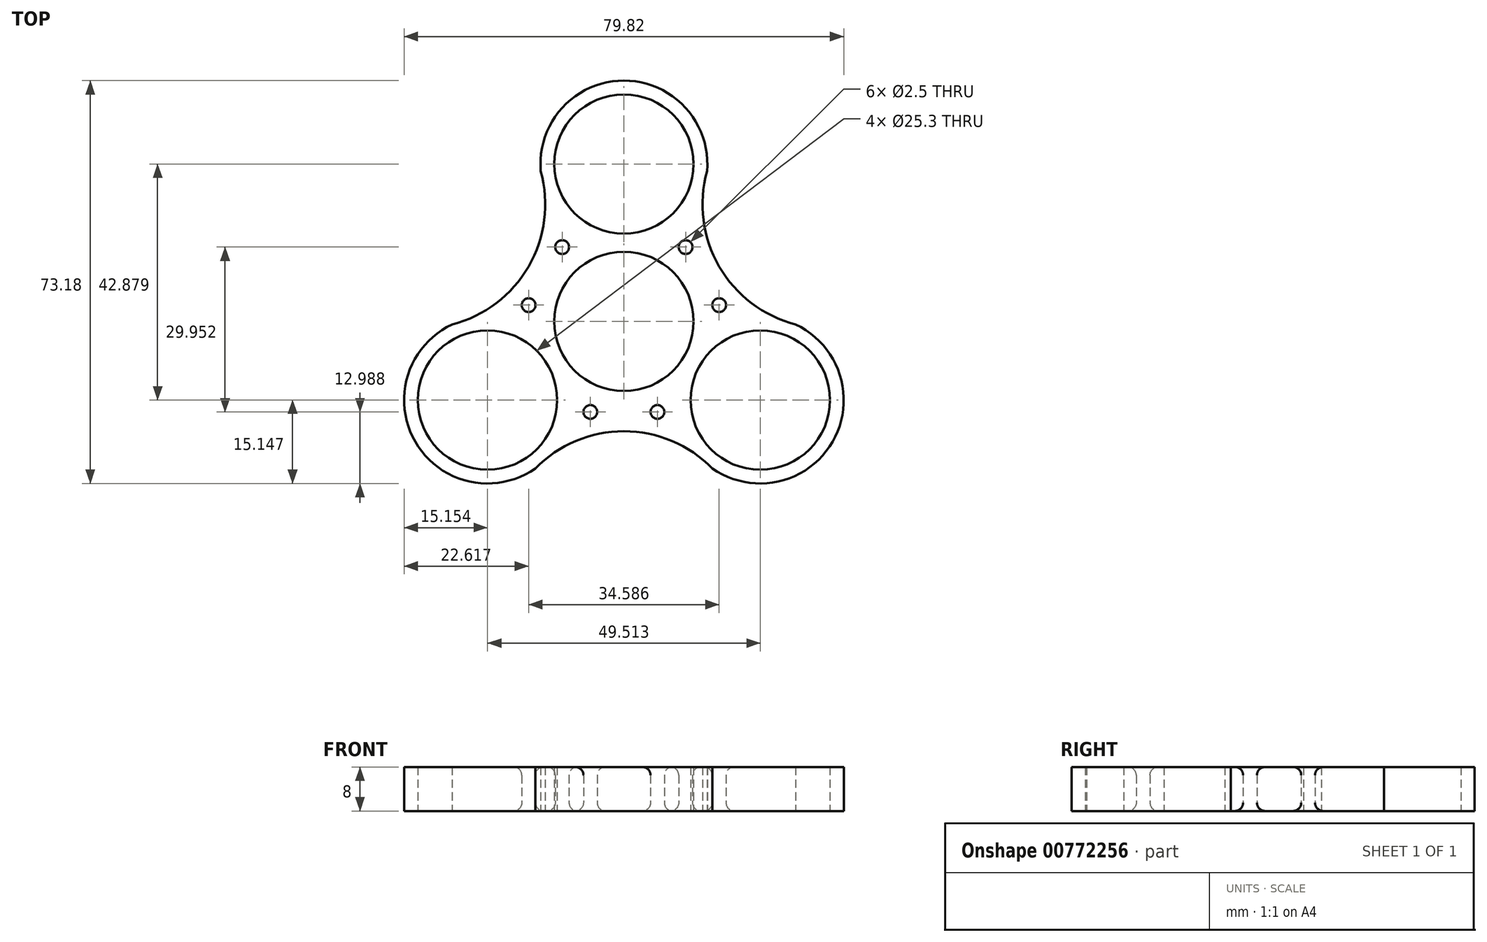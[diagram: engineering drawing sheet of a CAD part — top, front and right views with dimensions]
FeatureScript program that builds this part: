
annotation { "Feature Type Name" : "Feature", "Feature Type Description" : "" }
export const myFeature = defineFeature(function(context is Context, id is Id, definition is map)
    precondition{}
    {
        {
            var Q0;
            Q0=qCreatedBy(makeId("Top.planeOp"),FACE);
            var sketch = newSketch(context, id + "F0", { "sketchPlane" : qUnion([Q0])});
            skCircle(sketch, "E0", {"center": v(0, 0) * mm, "radius": 12.65 * mm});
            skCircle(sketch, "E1", {"center": v(0, 28.59) * mm, "radius": 12.65 * mm});
            skArc(sketch, "E2", {"start": v(14.44, 24.01) * mm, "mid": v(0, 43.74) * mm, "end": v(-14.44, 24.01) * mm});
            skPoint(sketch, "E3.start.orphan", {"position": v(-15.15, 0) * mm});
            skCircle(sketch, "E4.1.0", {"center": v(-24.76, -14.3) * mm, "radius": 12.65 * mm});
            skArc(sketch, "E4.1.1", {"start": v(-28.02, 0.5) * mm, "mid": v(-37.88, -21.87) * mm, "end": v(-13.58, -24.52) * mm});
            skCircle(sketch, "E4.2.0", {"center": v(24.76, -14.3) * mm, "radius": 12.65 * mm});
            skArc(sketch, "E4.2.1", {"start": v(13.58, -24.52) * mm, "mid": v(37.88, -21.87) * mm, "end": v(28.02, 0.5) * mm});
            skLineSegment(sketch, "E5", {"start": v(-14.89, -2.8) * mm, "end": v(-5.02, 14.3) * mm, "construction": true});
            skLineSegment(sketch, "E6", {"start": v(-9.96, 5.75) * mm, "end": v(-23.13, 13.35) * mm, "construction": true});
            skLineSegment(sketch, "E7", {"start": v(-23.13, 13.35) * mm, "end": v(-15.1, 27.27) * mm, "construction": true});
            skLineSegment(sketch, "E8", {"start": v(-23.13, 13.35) * mm, "end": v(-31.17, -0.57) * mm, "construction": true});
            skArc(sketch, "E9", {"start": v(-31.17, -0.57) * mm, "mid": v(-17.3, 9.98) * mm, "end": v(-15.1, 27.27) * mm});
            skArc(sketch, "E10.1.0", {"start": v(16.07, -26.7) * mm, "mid": v(0, -19.97) * mm, "end": v(-16.07, -26.7) * mm});
            skArc(sketch, "E10.2.0", {"start": v(15.1, 27.27) * mm, "mid": v(17.3, 9.98) * mm, "end": v(31.17, -0.57) * mm});
            skPoint(sketch, "E11.center.orphan", {"position": v(-17.3, 9.98) * mm});
            skLineSegment(sketch, "E12", {"start": v(-17.3, 9.98) * mm, "end": v(-17.3, -4.08) * mm, "construction": true});
            skCircle(sketch, "E13", {"center": v(-17.3, 2.95) * mm, "radius": 1.25 * mm});
            skCircle(sketch, "E14.1.0", {"center": v(6.09, -16.45) * mm, "radius": 1.25 * mm});
            skCircle(sketch, "E14.2.0", {"center": v(11.2, 13.5) * mm, "radius": 1.25 * mm});
            skLineSegment(sketch, "E15", {"start": v(-17.3, 2.95) * mm, "end": v(23.66, 2.95) * mm, "construction": true});
            skArc(sketch, "E16", {"start": v(17.3, 8.66) * mm, "mid": v(17.65, 8.71) * mm, "end": v(17.99, 8.86) * mm});
            skLineSegment(sketch, "E17", {"start": v(17.3, 9.98) * mm, "end": v(17.3, 2.95) * mm, "construction": true});
            skCircle(sketch, "E18", {"center": v(17.3, 2.95) * mm, "radius": 1.25 * mm});
            skCircle(sketch, "E19.1.0", {"center": v(-11.2, 13.5) * mm, "radius": 1.25 * mm});
            skCircle(sketch, "E19.2.0", {"center": v(-6.09, -16.45) * mm, "radius": 1.25 * mm});
            skSolve(sketch);
        }
        {
            var Q0;
            Q0=makeQuery(id+"F0.imprint","IMPRINT",FACE,{"disambiguationData":[TD([[makeQuery(id+"F0.imprint","IMPRINT",EDGE,{"derivedFrom":sQuery(id+"F0.wireOp",EDGE,"E0")}),-1.0]])]});
            extrude(context, id + "F1", {"entities" : qUnion([Q0]), "depth" : 8 * mm, "offsetDistance" : 25 * mm});
        }
        {
            var Q0;
            Q0=makeQuery(id+"F1.opExtrude","CAP_EDGE",EDGE,{"disambiguationData":[OSD([sQuery(id+"F0.wireOp",EDGE,"E19.1.0")])],"isStart":true});
            var Q1;
            Q1=makeQuery(id+"F1.opExtrude","CAP_EDGE",EDGE,{"disambiguationData":[OSD([sQuery(id+"F0.wireOp",EDGE,"E19.1.0")])],"isStart":false});
            var Q2;
            Q2=makeQuery(id+"F1.opExtrude","CAP_EDGE",EDGE,{"disambiguationData":[OSD([sQuery(id+"F0.wireOp",EDGE,"E13")])],"isStart":false});
            var Q3;
            Q3=makeQuery(id+"F1.opExtrude","CAP_EDGE",EDGE,{"disambiguationData":[OSD([sQuery(id+"F0.wireOp",EDGE,"E19.2.0")])],"isStart":false});
            var Q4;
            Q4=makeQuery(id+"F1.opExtrude","CAP_EDGE",EDGE,{"disambiguationData":[OSD([sQuery(id+"F0.wireOp",EDGE,"E14.1.0")])],"isStart":false});
            var Q5;
            Q5=makeQuery(id+"F1.opExtrude","CAP_EDGE",EDGE,{"disambiguationData":[OSD([sQuery(id+"F0.wireOp",EDGE,"E18")])],"isStart":false});
            var Q6;
            Q6=makeQuery(id+"F1.opExtrude","CAP_EDGE",EDGE,{"disambiguationData":[OSD([sQuery(id+"F0.wireOp",EDGE,"E14.2.0")])],"isStart":true});
            var Q7;
            Q7=makeQuery(id+"F1.opExtrude","CAP_EDGE",EDGE,{"disambiguationData":[OSD([sQuery(id+"F0.wireOp",EDGE,"E14.2.0")])],"isStart":false});
            var Q8;
            Q8=makeQuery(id+"F1.opExtrude","CAP_EDGE",EDGE,{"disambiguationData":[OSD([sQuery(id+"F0.wireOp",EDGE,"E19.2.0")])],"isStart":true});
            var Q9;
            Q9=makeQuery(id+"F1.opExtrude","CAP_EDGE",EDGE,{"disambiguationData":[OSD([sQuery(id+"F0.wireOp",EDGE,"E14.1.0")])],"isStart":true});
            var Q10;
            Q10=makeQuery(id+"F1.opExtrude","CAP_EDGE",EDGE,{"disambiguationData":[OSD([sQuery(id+"F0.wireOp",EDGE,"E13")])],"isStart":true});
            var Q11;
            Q11=makeQuery(id+"F1.opExtrude","CAP_EDGE",EDGE,{"disambiguationData":[OSD([sQuery(id+"F0.wireOp",EDGE,"E18")])],"isStart":true});
            fillet(context, id + "F2", {"entities" : qUnion([Q0, Q1, Q2, Q3, Q4, Q5, Q6, Q7, Q8, Q9, Q10, Q11]), "radius" : 1.5 * mm, "tangentPropagation" : true, "allowEdgeOverflow" : false});
        }
    });
